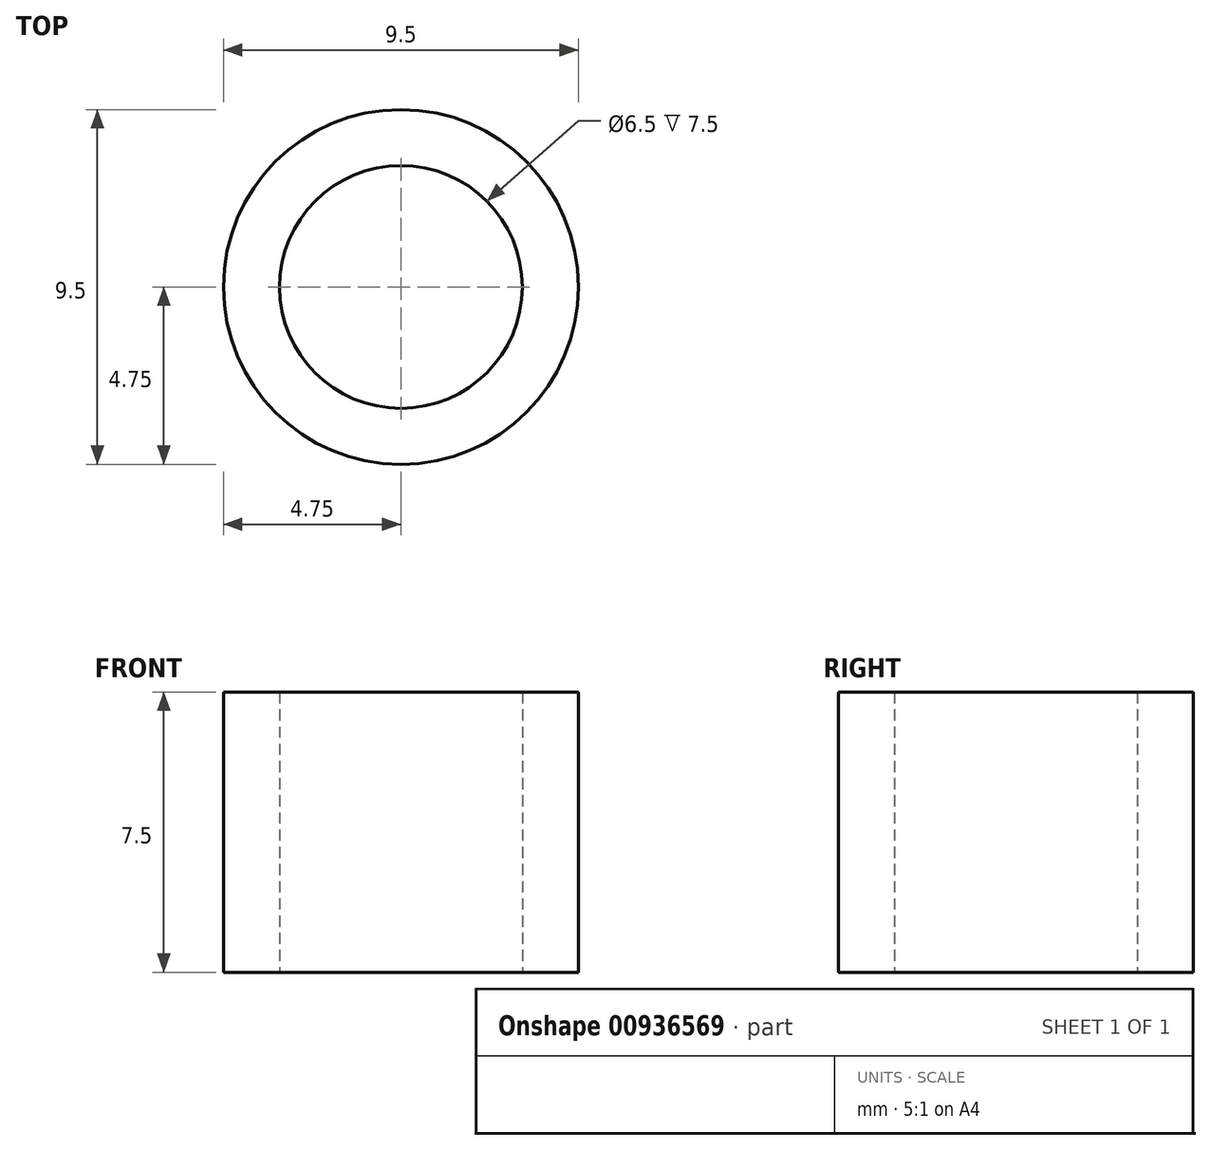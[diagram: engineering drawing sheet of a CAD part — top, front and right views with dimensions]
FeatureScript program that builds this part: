
annotation { "Feature Type Name" : "Feature", "Feature Type Description" : "" }
export const myFeature = defineFeature(function(context is Context, id is Id, definition is map)
    precondition{}
    {
        {
            var Q0;
            Q0=qCreatedBy(makeId("Top.planeOp"),FACE);
            var sketch = newSketch(context, id + "F0", { "sketchPlane" : qUnion([Q0])});
            skCircle(sketch, "E0", {"center": v(0, 0) * mm, "radius": 3.25 * mm});
            skCircle(sketch, "E1", {"center": v(0, 0) * mm, "radius": 4.75 * mm});
            skSolve(sketch);
        }
        {
            var Q0;
            Q0 = qSketchRegion(id + "F0", true);
            extrude(context, id + "F1", {"entities" : qUnion([Q0]), "depth" : 7.5 * mm, "offsetDistance" : 25 * mm});
        }
    });
